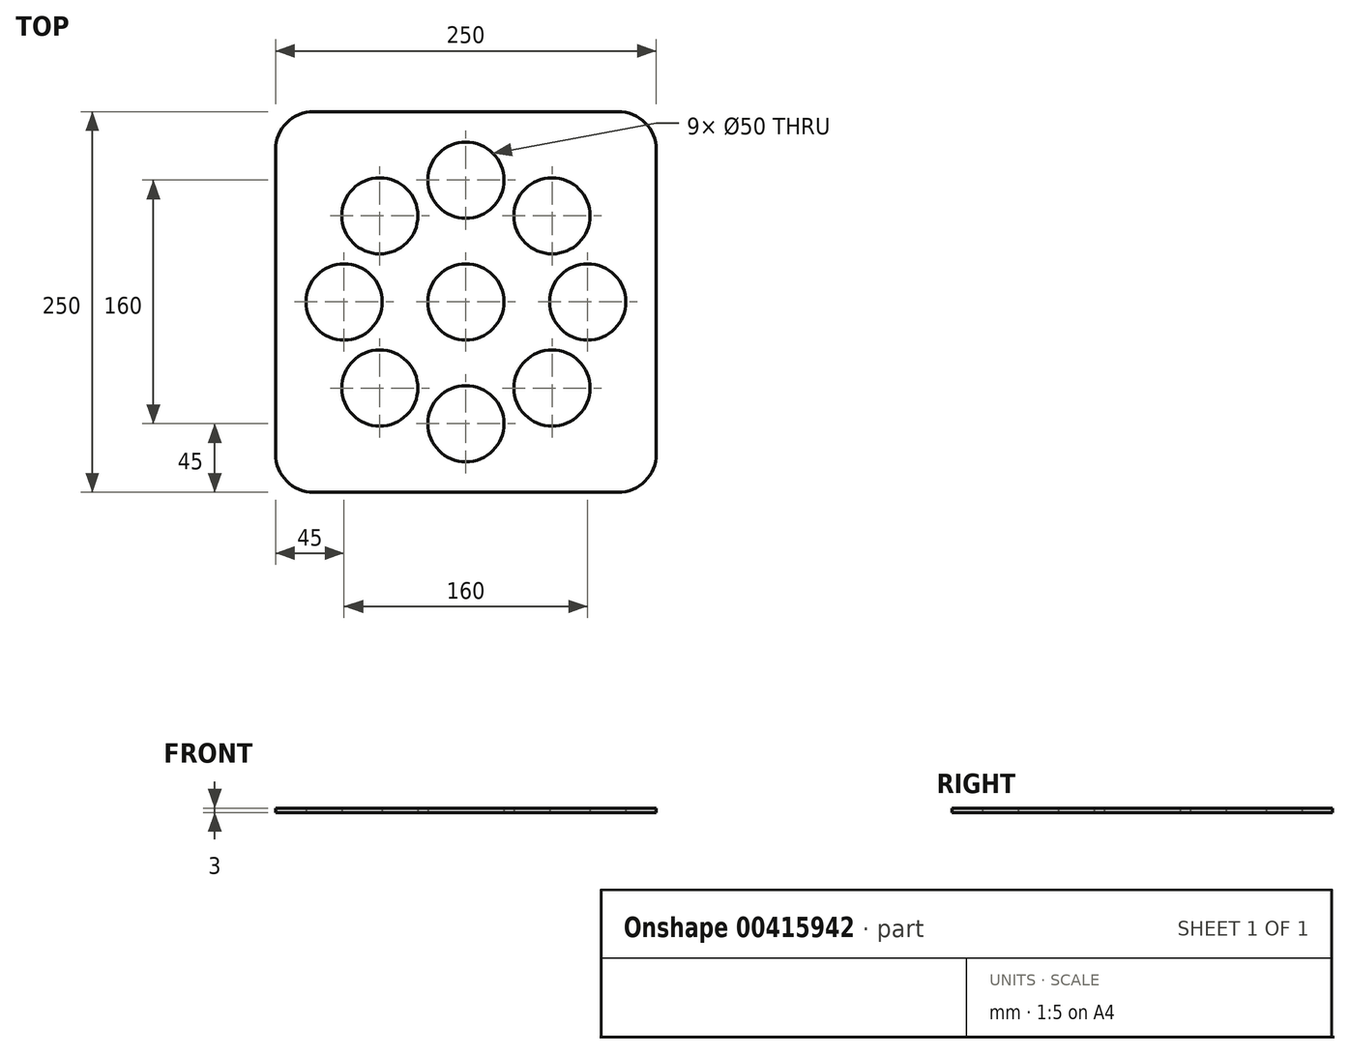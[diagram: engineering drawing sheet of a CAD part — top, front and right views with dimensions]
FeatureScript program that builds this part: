
annotation { "Feature Type Name" : "Feature", "Feature Type Description" : "" }
export const myFeature = defineFeature(function(context is Context, id is Id, definition is map)
    precondition{}
    {
        {
            var Q0;
            Q0=qCreatedBy(makeId("Top.planeOp"),FACE);
            var sketch = newSketch(context, id + "F0", { "sketchPlane" : qUnion([Q0])});
            skLineSegment(sketch, "E0.bottom", {"start": v(100, 125) * mm, "end": v(-100, 125) * mm});
            skLineSegment(sketch, "E0.top", {"start": v(100, -125) * mm, "end": v(-100, -125) * mm});
            skLineSegment(sketch, "E0.left", {"start": v(125, 100) * mm, "end": v(125, -100) * mm});
            skLineSegment(sketch, "E0.right", {"start": v(-125, 100) * mm, "end": v(-125, -100) * mm});
            skPoint(sketch, "E0.middle", {"position": v(0, 0) * mm});
            skCircle(sketch, "E1", {"center": v(0, 0) * mm, "radius": 25 * mm});
            skCircle(sketch, "E2", {"center": v(0, 80) * mm, "radius": 25 * mm});
            skCircle(sketch, "E3.1.0", {"center": v(-56.57, 56.57) * mm, "radius": 25 * mm});
            skCircle(sketch, "E3.2.0", {"center": v(-80, 0) * mm, "radius": 25 * mm});
            skCircle(sketch, "E3.3.0", {"center": v(-56.57, -56.57) * mm, "radius": 25 * mm});
            skCircle(sketch, "E3.4.0", {"center": v(0, -80) * mm, "radius": 25 * mm});
            skCircle(sketch, "E3.5.0", {"center": v(56.57, -56.57) * mm, "radius": 25 * mm});
            skCircle(sketch, "E3.6.0", {"center": v(80, 0) * mm, "radius": 25 * mm});
            skCircle(sketch, "E3.7.0", {"center": v(56.57, 56.57) * mm, "radius": 25 * mm});
            skPoint(sketch, "E4.visualSharp", {"position": v(-125, 125) * mm});
            skArc(sketch, "E4.filletArc", {"start": v(-100, 125) * mm, "mid": v(-117.68, 117.68) * mm, "end": v(-125, 100) * mm});
            skPoint(sketch, "E5.visualSharp", {"position": v(125, 125) * mm});
            skArc(sketch, "E5.filletArc", {"start": v(125, 100) * mm, "mid": v(117.68, 117.68) * mm, "end": v(100, 125) * mm});
            skPoint(sketch, "E6.visualSharp", {"position": v(125, -125) * mm});
            skArc(sketch, "E6.filletArc", {"start": v(100, -125) * mm, "mid": v(117.68, -117.68) * mm, "end": v(125, -100) * mm});
            skPoint(sketch, "E7.visualSharp", {"position": v(-125, -125) * mm});
            skArc(sketch, "E7.filletArc", {"start": v(-125, -100) * mm, "mid": v(-117.68, -117.68) * mm, "end": v(-100, -125) * mm});
            skSolve(sketch);
        }
        {
            var Q0;
            Q0 = qSketchRegion(id + "F0", true);
            extrude(context, id + "F1", {"entities" : qUnion([Q0]), "depth" : 3 * mm});
        }
    });
